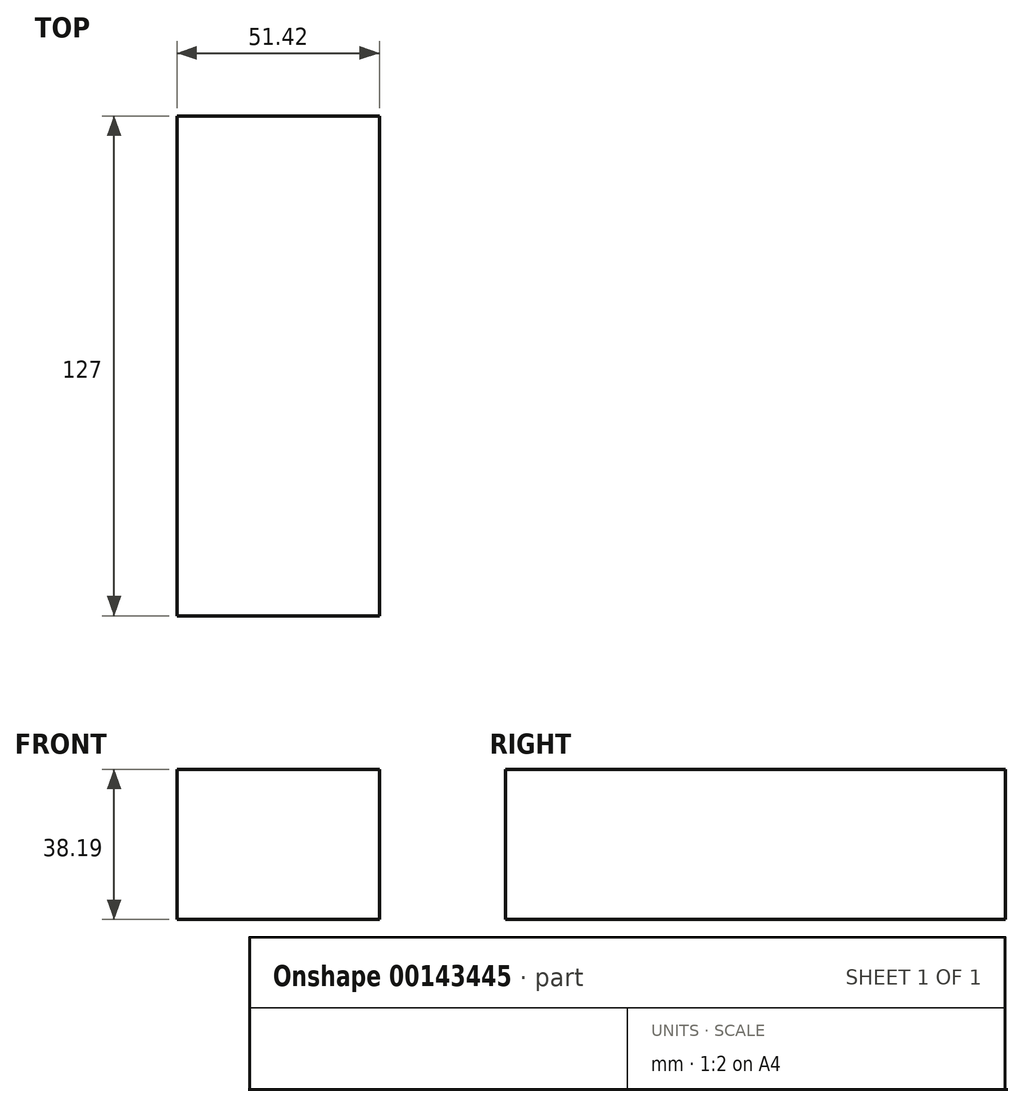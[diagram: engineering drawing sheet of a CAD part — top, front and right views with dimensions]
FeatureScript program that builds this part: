
annotation { "Feature Type Name" : "Feature", "Feature Type Description" : "" }
export const myFeature = defineFeature(function(context is Context, id is Id, definition is map)
    precondition{}
    {
        {
            var Q0;
            Q0=qCreatedBy(makeId("Front.planeOp"),FACE);
            var sketch = newSketch(context, id + "F0", { "sketchPlane" : qUnion([Q0])});
            skLineSegment(sketch, "E0.bottom", {"start": v(0, 0) * mm, "end": v(-51.42, 0) * mm});
            skLineSegment(sketch, "E0.top", {"start": v(0, 38.19) * mm, "end": v(-51.42, 38.19) * mm});
            skLineSegment(sketch, "E0.left", {"start": v(0, 0) * mm, "end": v(0, 38.19) * mm});
            skLineSegment(sketch, "E0.right", {"start": v(-51.42, 0) * mm, "end": v(-51.42, 38.19) * mm});
            skSolve(sketch);
        }
        {
            var Q0;
            Q0=makeQuery(id+"F0.imprint","IMPRINT",FACE,{"disambiguationData":[TD([[makeQuery(id+"F0.imprint","IMPRINT",EDGE,{"derivedFrom":sQuery(id+"F0.wireOp",EDGE,"E0.bottom")}),-1.0]])]});
            extrude(context, id + "F1", {"entities" : qUnion([Q0]), "endBound" : BoundingType.SYMMETRIC, "depth" : 127 * mm});
        }
    });
